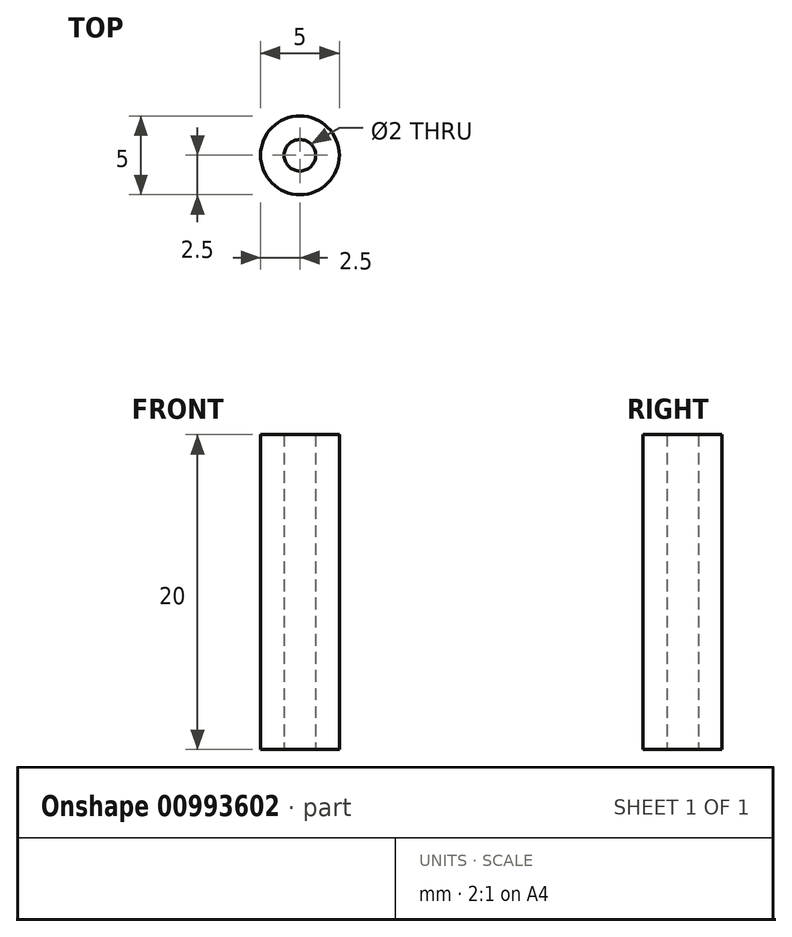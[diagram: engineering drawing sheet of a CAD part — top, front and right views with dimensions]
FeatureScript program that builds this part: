
annotation { "Feature Type Name" : "Feature", "Feature Type Description" : "" }
export const myFeature = defineFeature(function(context is Context, id is Id, definition is map)
    precondition{}
    {
        {
            var Q0;
            Q0=qCreatedBy(makeId("Top.planeOp"),FACE);
            var sketch = newSketch(context, id + "F0", { "sketchPlane" : qUnion([Q0])});
            skCircle(sketch, "E0", {"center": v(0, 0) * mm, "radius": 2.5 * mm});
            skCircle(sketch, "E1", {"center": v(0, 0) * mm, "radius": 1 * mm});
            skSolve(sketch);
        }
        {
            var Q0;
            Q0=makeQuery(id+"F0.imprint","IMPRINT",FACE,{"disambiguationData":[TD([[makeQuery(id+"F0.imprint","IMPRINT",EDGE,{"derivedFrom":sQuery(id+"F0.wireOp",EDGE,"E0")}),1.0]])]});
            extrude(context, id + "F1", {"entities" : qUnion([Q0]), "depth" : 20 * mm, "offsetDistance" : 25 * mm});
        }
    });
